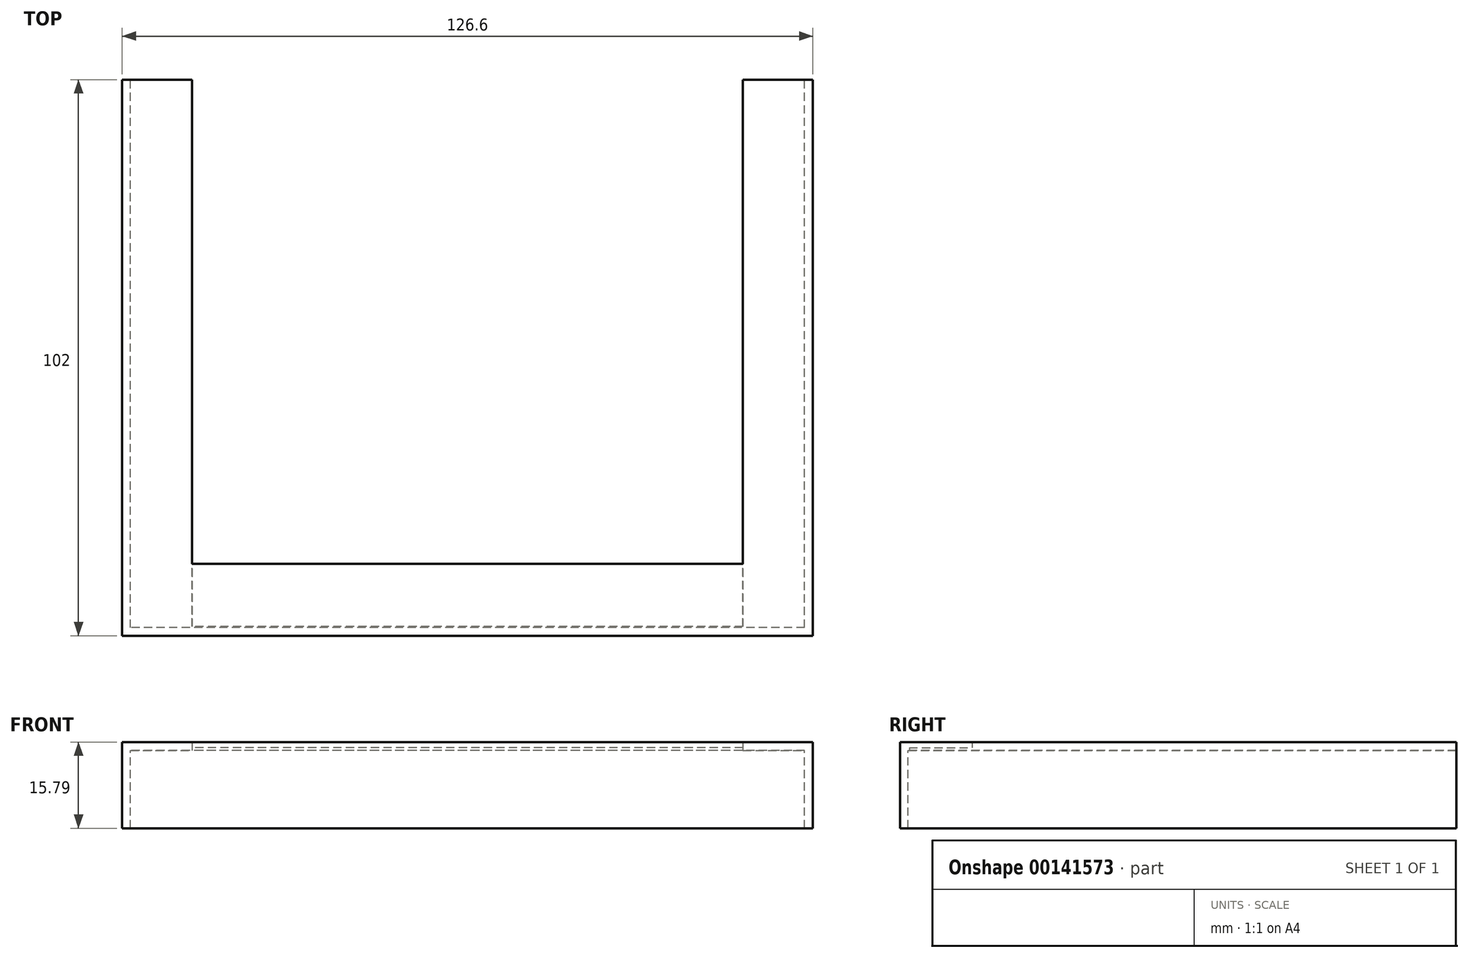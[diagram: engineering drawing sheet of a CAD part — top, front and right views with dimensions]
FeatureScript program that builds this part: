
annotation { "Feature Type Name" : "Feature", "Feature Type Description" : "" }
export const myFeature = defineFeature(function(context is Context, id is Id, definition is map)
    precondition{}
    {
        {
            assignVariable(context, id + "F0", {"name" : "w", "anyValue" : 1.5});
        }
        {
            var Q0;
            Q0=qCreatedBy(makeId("Top.planeOp"),FACE);
            var sketch = newSketch(context, id + "F1", { "sketchPlane" : qUnion([Q0])});
            skLineSegment(sketch, "E0.top", {"start": v(64.43, -49.72) * mm, "end": v(-62.17, -49.72) * mm});
            skLineSegment(sketch, "E0.left", {"start": v(64.43, 52.28) * mm, "end": v(64.43, -49.72) * mm});
            skLineSegment(sketch, "E0.right", {"start": v(-62.17, 52.28) * mm, "end": v(-62.17, -49.72) * mm});
            skPoint(sketch, "E0.middle", {"position": v(0, 0) * mm});
            skLineSegment(sketch, "E1.bottom", {"start": v(62.93, -48.22) * mm, "end": v(-60.67, -48.22) * mm});
            skLineSegment(sketch, "E1.left", {"start": v(62.93, -48.22) * mm, "end": v(62.93, 52.28) * mm});
            skLineSegment(sketch, "E1.right", {"start": v(-60.67, -48.22) * mm, "end": v(-60.67, 52.28) * mm});
            skLineSegment(sketch, "E2", {"start": v(-60.67, 52.28) * mm, "end": v(-62.17, 52.28) * mm});
            skLineSegment(sketch, "E3", {"start": v(64.43, 52.28) * mm, "end": v(62.93, 52.28) * mm});
            skLineSegment(sketch, "E4", {"start": v(-60.67, 52.28) * mm, "end": v(62.93, 52.28) * mm, "construction": true});
            skLineSegment(sketch, "E5", {"start": v(-60.28, -48.22) * mm, "end": v(-60.28, -49.72) * mm, "construction": true});
            skLineSegment(sketch, "E6", {"start": v(-60.67, -37.67) * mm, "end": v(-62.17, -37.67) * mm, "construction": true});
            skLineSegment(sketch, "E7", {"start": v(59.65, -48.22) * mm, "end": v(59.65, -49.72) * mm, "construction": true});
            skLineSegment(sketch, "E8", {"start": v(62.93, -44.04) * mm, "end": v(64.43, -44.04) * mm, "construction": true});
            skLineSegment(sketch, "E9", {"start": v(62.93, 46.55) * mm, "end": v(64.43, 46.55) * mm, "construction": true});
            skLineSegment(sketch, "E10", {"start": v(-62.17, 35.04) * mm, "end": v(-60.67, 35.04) * mm, "construction": true});
            skSolve(sketch);
        }
        {
            var Q0;
            Q0 = qSketchRegion(id + "F1", true);
            extrude(context, id + "F2", {"entities" : qUnion([Q0]), "oppositeDirection" : true, "depth" : 14.29 * mm});
        }
        {
            var Q0;
            Q0=makeQuery(id+"F2.opExtrude","CAP_FACE",FACE,{"disambiguationData":[OSD([sQuery(id+"F1.wireOp",EDGE,"E0.top"),sQuery(id+"F1.wireOp",EDGE,"E0.left"),sQuery(id+"F1.wireOp",EDGE,"E0.right"),sQuery(id+"F1.wireOp",EDGE,"E1.bottom"),sQuery(id+"F1.wireOp",EDGE,"E1.left"),sQuery(id+"F1.wireOp",EDGE,"E1.right"),sQuery(id+"F1.wireOp",EDGE,"fF0X1MJX-YYdu-bKVt-9Q5G-taucXDst0xRZ"),sQuery(id+"F1.wireOp",EDGE,"E2"),sQuery(id+"F1.wireOp",EDGE,"E3"),sQuery(id+"F1.wireOp",EDGE,"aIOaIurB-2IZl-XgVS-8yGW-H7bNG8F0PKCH")])],"isStart":true});
            var sketch = newSketch(context, id + "F3", { "sketchPlane" : qUnion([Q0])});
            skLineSegment(sketch, "E11.bottom", {"start": v(-62.17, -49.72) * mm, "end": v(64.43, -49.72) * mm});
            skLineSegment(sketch, "E11.top", {"start": v(-62.17, 52.28) * mm, "end": v(-49.37, 52.28) * mm});
            skLineSegment(sketch, "E11.left", {"start": v(-62.17, -49.72) * mm, "end": v(-62.17, 52.28) * mm});
            skLineSegment(sketch, "E11.right", {"start": v(64.43, -49.72) * mm, "end": v(64.43, 52.28) * mm});
            skLineSegment(sketch, "E12.top", {"start": v(-62.17, -49.72) * mm, "end": v(-49.37, -49.72) * mm});
            skLineSegment(sketch, "E12.left", {"start": v(-62.17, 52.28) * mm, "end": v(-62.17, -49.72) * mm});
            skLineSegment(sketch, "E12.right", {"start": v(-49.37, 52.28) * mm, "end": v(-49.37, -36.5) * mm});
            skLineSegment(sketch, "E13.bottom", {"start": v(51.63, 52.28) * mm, "end": v(64.43, 52.28) * mm});
            skLineSegment(sketch, "E13.top", {"start": v(51.63, -49.72) * mm, "end": v(64.43, -49.72) * mm});
            skLineSegment(sketch, "E13.left", {"start": v(51.63, 52.28) * mm, "end": v(51.63, -36.5) * mm});
            skLineSegment(sketch, "E13.right", {"start": v(64.43, 52.28) * mm, "end": v(64.43, -49.72) * mm});
            skLineSegment(sketch, "E14.bottom", {"start": v(64.43, -49.72) * mm, "end": v(-62.17, -49.72) * mm});
            skLineSegment(sketch, "E14.top", {"start": v(51.63, -36.5) * mm, "end": v(-49.37, -36.5) * mm});
            skLineSegment(sketch, "E14.left", {"start": v(64.43, -49.72) * mm, "end": v(64.43, -36.5) * mm});
            skLineSegment(sketch, "E14.right", {"start": v(-62.17, -49.72) * mm, "end": v(-62.17, -36.5) * mm});
            skSolve(sketch);
        }
        {
            var Q0;
            Q0 = qSketchRegion(id + "F3", true);
            extrude(context, id + "F4", {"entities" : qUnion([Q0]), "operationType" : NewBodyOperationType.ADD, "depth" : (getVariable(context, 'w')) * mm});
        }
        {
            var Q0;
            Q0=makeQuery(id+"F4.opExtrude","SWEPT_FACE",FACE,{"disambiguationData":[OSD([sQuery(id+"F3.wireOp",EDGE,"E14.top")])]});
            var sketch = newSketch(context, id + "F5", { "sketchPlane" : qUnion([Q0])});
            skLineSegment(sketch, "E15.bottom", {"start": v(-51.63, 0) * mm, "end": v(51.37, 0) * mm});
            skLineSegment(sketch, "E15.top", {"start": v(-51.63, 0.5) * mm, "end": v(51.37, 0.5) * mm});
            skLineSegment(sketch, "E15.left", {"start": v(-51.63, -0.4) * mm, "end": v(-51.63, 0.5) * mm});
            skLineSegment(sketch, "E15.right", {"start": v(51.37, 0) * mm, "end": v(51.37, 0.5) * mm});
            skSolve(sketch);
        }
        {
            var Q0;
            {var subQ0=sQuery(id+"F5.wireOp",EDGE,"E15.bottom");var subQ1=sQuery(id+"F3.wireOp",EDGE,"E14.top");var subQ2=makeQuery(id+"F4.opExtrude","SWEPT_EDGE",EDGE,{"disambiguationData":[OSD([sQuery(id+"F3.wireOp",EDGE,"E12.right"),subQ1])]});var subQ3=makeQuery(id+"F5.imprint","INTERSECT",VERTEX,{"derivedFrom":[subQ2,subQ0]});Q0=makeQuery(id+"F5.imprint","IMPRINT",FACE,{"disambiguationData":[TD([[makeQuery(id+"F5.imprint","IMPRINT",EDGE,{"disambiguationData":[TD([[subQ3,1.0]])],"derivedFrom":subQ0}),1.0]])]});}
            extrude(context, id + "F6", {"entities" : qUnion([Q0]), "operationType" : NewBodyOperationType.REMOVE, "oppositeDirection" : true, "depth" : 11.5 * mm});
        }
    });
